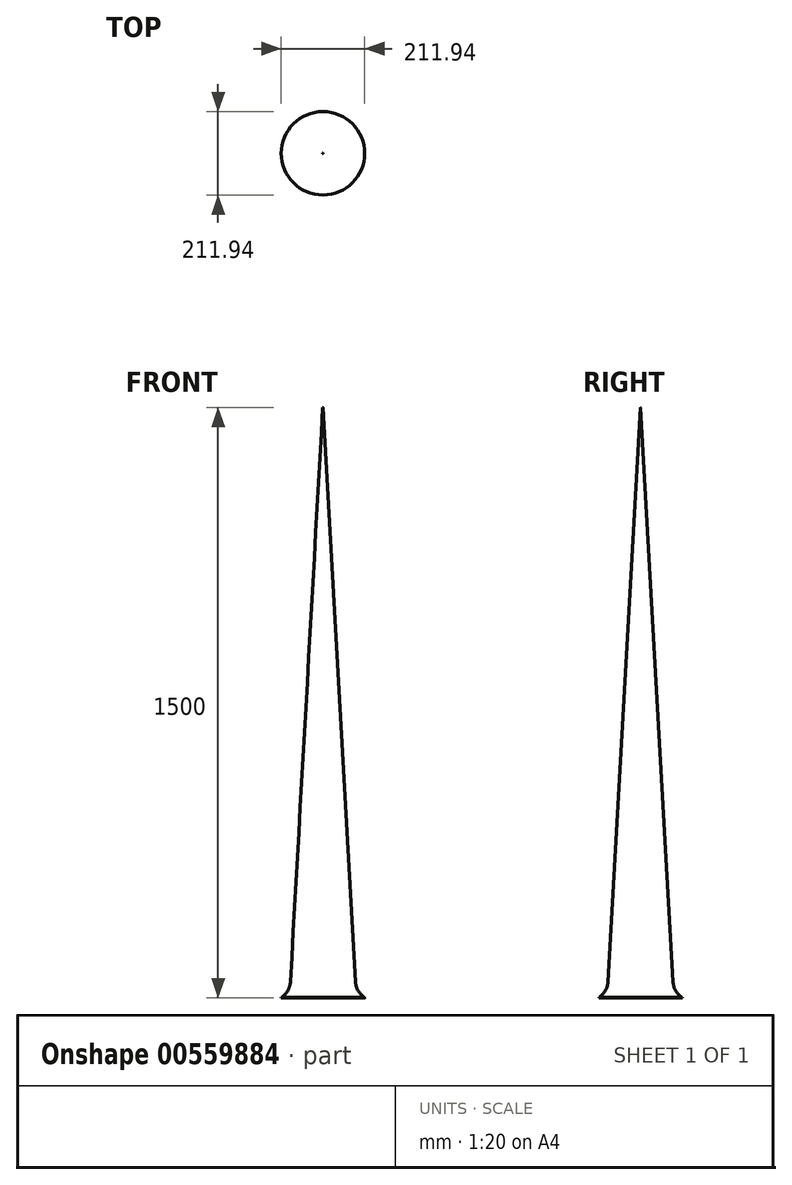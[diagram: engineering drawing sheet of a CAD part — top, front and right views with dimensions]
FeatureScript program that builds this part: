
annotation { "Feature Type Name" : "Feature", "Feature Type Description" : "" }
export const myFeature = defineFeature(function(context is Context, id is Id, definition is map)
    precondition{}
    {
        {
            var Q0;
            Q0=qCreatedBy(makeId("Top.planeOp"),FACE);
            var sketch = newSketch(context, id + "F0", { "sketchPlane" : qUnion([Q0])});
            skCircle(sketch, "E0", {"center": v(0, 0) * mm, "radius": 85 * mm});
            skSolve(sketch);
        }
        {
            var Q0;
            Q0=qCreatedBy(makeId("Top.planeOp"),FACE);
            cPlane(context, id + "F1", {"entities" : qUnion([Q0]), "cplaneType" : CPlaneType.OFFSET, "offset" : 1500 * mm, "width" : 150 * mm, "height" : 150 * mm});
        }
        {
            var Q0;
            Q0=qCreatedBy(id+"F1.planeOp",FACE);
            var sketch = newSketch(context, id + "F2", { "sketchPlane" : qUnion([Q0])});
            skCircle(sketch, "E1", {"center": v(0, 0) * mm, "radius": 0.5 * mm});
            skSolve(sketch);
        }
        {
            var Q0;
            Q0=makeQuery(id+"F0.imprint","IMPRINT",FACE,{"disambiguationData":[TD([[makeQuery(id+"F0.imprint","IMPRINT",EDGE,{"derivedFrom":sQuery(id+"F0.wireOp",EDGE,"E0")}),1.0]])]});
            var Q1;
            Q1 = qSketchRegion(id + "F2", true);
            loft(context, id + "F3", {"sheetProfilesArray" : [{ "sheetProfileEntities" : qUnion([Q0]) }, { "sheetProfileEntities" : qUnion([Q1]) }]});
        }
        {
            var Q0;
            Q0=qCreatedBy(makeId("Top.planeOp"),FACE);
            var sketch = newSketch(context, id + "F4", { "sketchPlane" : qUnion([Q0])});
            skCircle(sketch, "E2", {"center": v(0, 0) * mm, "radius": 105.97 * mm});
            skSolve(sketch);
        }
        {
            var Q0;
            Q0 = qSketchRegion(id + "F4", true);
            extrude(context, id + "F5", {"entities" : qUnion([Q0]), "operationType" : NewBodyOperationType.ADD, "depth" : 1 * mm, "offsetDistance" : 25 * mm});
        }
        {
            var Q0;
            Q0=makeQuery(id+"F5.boolean.opBoolean","INTERSECT",EDGE,{"derivedFrom":[makeQuery(id+"F3.opLoft","SWEPT_FACE",FACE,{"disambiguationData":[OSD([sQuery(id+"F0.wireOp",EDGE,"E0"),sQuery(id+"F2.wireOp",EDGE,"E1")])]}),makeQuery(id+"F5.opExtrude","CAP_FACE",FACE,{"disambiguationData":[OSD([sQuery(id+"F4.wireOp",EDGE,"E2")])],"isStart":false})]});
            fillet(context, id + "F6", {"entities" : qUnion([Q0]), "radius" : 50 * mm, "tangentPropagation" : true, "allowEdgeOverflow" : false});
        }
    });
